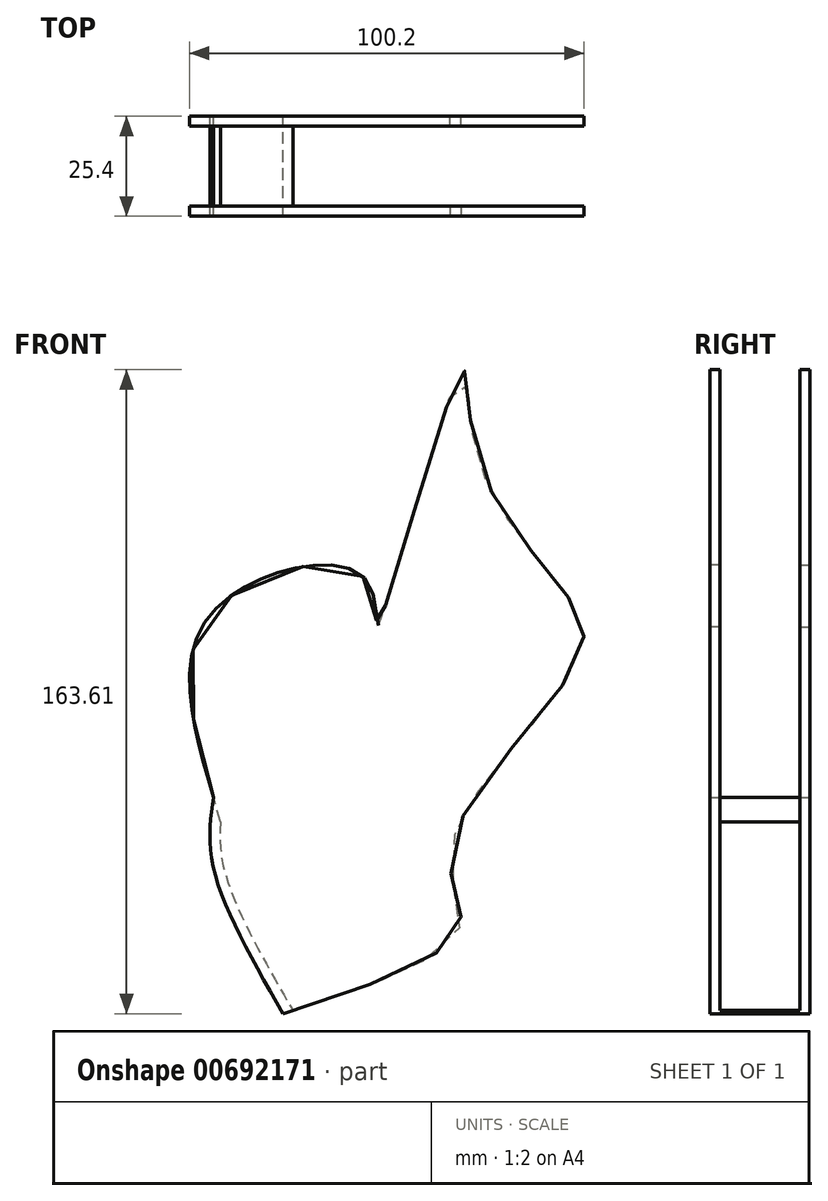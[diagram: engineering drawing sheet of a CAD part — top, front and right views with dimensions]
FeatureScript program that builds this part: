
annotation { "Feature Type Name" : "Feature", "Feature Type Description" : "" }
export const myFeature = defineFeature(function(context is Context, id is Id, definition is map)
    precondition{}
    {
        {
            var Q0;
            Q0=qCreatedBy(makeId("Front.planeOp"),FACE);
            var sketch = newSketch(context, id + "F0", { "sketchPlane" : qUnion([Q0])});
            skFitSpline(sketch, "E0", {"points": [v(0, 0) * mm, v(0, 47.31) * mm, v(38.87, 55.21) * mm, v(41.77, 43.36) * mm, v(62.88, 108.23) * mm, v(66.85, 87.27) * mm, v(90.22, 50.79) * mm, v(92.2, 34.1) * mm, v(60.33, -12.54) * mm, v(62.55, -32.88) * mm, v(17.7, -54.93) * mm], "startDerivative": vector(-136, 462.48) * mm, "endDerivative": vector(-529.28, -168.89) * mm});
            skFitSpline(sketch, "E1", {"points": [v(0, 0) * mm, v(0, -17.85) * mm, v(17.7, -54.93) * mm], "startDerivative": vector(-5.83, -41.64) * mm, "endDerivative": vector(38.21, -66.52) * mm});
            skSolve(sketch);
        }
        {
            var Q0;
            Q0 = qSketchRegion(id + "F0", true);
            extrude(context, id + "F1", {"entities" : qUnion([Q0]), "depth" : 25.4 * mm, "offsetDistance" : 25.4 * mm});
        }
        {
            var Q0;
            Q0=makeQuery(id+"F1.opExtrude","SWEPT_FACE",FACE,{"disambiguationData":[OSD([sQuery(id+"F0.wireOp",EDGE,"E0")])]});
            shell(context, id + "F2", {"entities" : qUnion([Q0]), "thickness" : 2.54 * mm});
        }
    });
